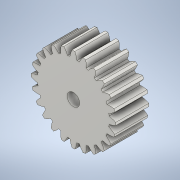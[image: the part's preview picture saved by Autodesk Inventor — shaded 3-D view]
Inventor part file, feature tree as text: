
AUTODESK INVENTOR PART (.ipt)
format: ipt  version: 2021 (Build 250183000, 183)  size: 249,856 bytes
history: native  units: mm (DEFAULTED — no unit token found)
features: plane x3, other x3, sketch x3, extrude x1, hole x1
ambient origin geometry x8: Origin, YZ Plane, XZ Plane, XY Plane, X Axis, Y Axis, Z Axis, Center Point
bodies: Solid1 (feature_tree)
feature tree (11):
  extrude  "Extrusion1"  Depth=8.0mm TaperAngle=0.0deg
  plane  "Work Plane2"
  plane  "Work Plane8"
  plane  "Work Plane9"
  other  "Spur Gear"
  hole  "Hole1"  [1 undecoded]
  sketch  "Sketch1"  dims[d0=20.48mm d1=8.0mm d2=0.0mm]
  sketch  "Sketch2"  dims[d3=19.2mm d4=10.0mm d5=0.0mm]
  other  "Srf1"
  sketch  "Sketch3"  dims[d16=28.8mm d17=0.0mm d34=1.308997mm d39=0.0mm d41=0.0mm d43=28.8mm d46=28.8mm d47=0.0mm d48=0.0mm d49=3.0mm d50=3.0mm d51=6.0mm d52=4.0mm d53=2.0mm d54=90.0deg d55=8.0mm d56=20.594885mm]
  other  "Pitch Diameter"
note: 1 required parameter value undecoded (feature->parameter linkage not recoverable at this tier; creation-order binding heuristic only, values carry confidence <= 0.55)
